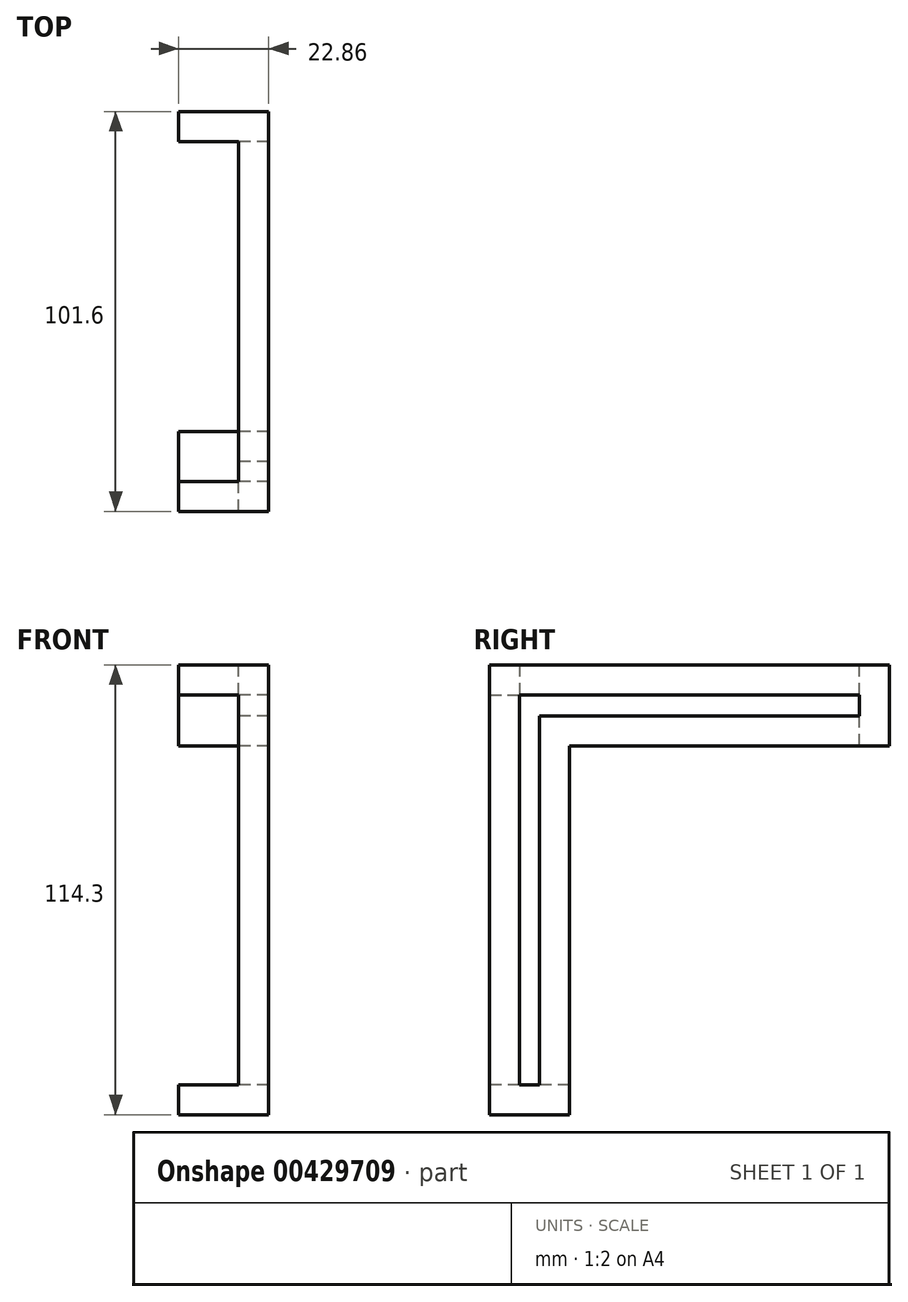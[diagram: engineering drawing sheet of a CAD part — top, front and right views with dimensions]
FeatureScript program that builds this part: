
annotation { "Feature Type Name" : "Feature", "Feature Type Description" : "" }
export const myFeature = defineFeature(function(context is Context, id is Id, definition is map)
    precondition{}
    {
        {
            var Q0;
            Q0=qCreatedBy(makeId("Right.planeOp"),FACE);
            var sketch = newSketch(context, id + "F0", { "sketchPlane" : qUnion([Q0])});
            skLineSegment(sketch, "E0.bottom", {"start": v(0, -114.3) * mm, "end": v(20.32, -114.3) * mm});
            skLineSegment(sketch, "E0.top", {"start": v(0, 0) * mm, "end": v(20.32, 0) * mm});
            skLineSegment(sketch, "E0.left", {"start": v(0, -114.3) * mm, "end": v(0, 0) * mm});
            skLineSegment(sketch, "E0.right", {"start": v(20.32, -114.3) * mm, "end": v(20.32, -20.57) * mm});
            skLineSegment(sketch, "E1.bottom", {"start": v(0, 0) * mm, "end": v(101.6, 0) * mm});
            skLineSegment(sketch, "E1.top", {"start": v(20.32, -20.57) * mm, "end": v(101.6, -20.57) * mm});
            skLineSegment(sketch, "E1.right", {"start": v(101.6, 0) * mm, "end": v(101.6, -20.57) * mm});
            skLineSegment(sketch, "E2", {"start": v(7.62, -106.68) * mm, "end": v(7.62, -7.62) * mm});
            skLineSegment(sketch, "E3", {"start": v(7.62, -7.62) * mm, "end": v(93.98, -7.62) * mm});
            skLineSegment(sketch, "E4", {"start": v(93.98, -7.62) * mm, "end": v(93.98, -12.95) * mm});
            skLineSegment(sketch, "E5", {"start": v(93.98, -12.95) * mm, "end": v(12.7, -12.95) * mm});
            skLineSegment(sketch, "E6", {"start": v(12.7, -12.95) * mm, "end": v(12.7, -106.68) * mm});
            skLineSegment(sketch, "E7", {"start": v(12.7, -106.68) * mm, "end": v(7.62, -106.68) * mm});
            skSolve(sketch);
        }
        {
            var Q0;
            Q0=makeQuery(id+"F0.imprint","IMPRINT",FACE,{"disambiguationData":[TD([[makeQuery(id+"F0.imprint","IMPRINT",EDGE,{"derivedFrom":sQuery(id+"F0.wireOp",EDGE,"E0.bottom")}),1.0]])]});
            extrude(context, id + "F1", {"entities" : qUnion([Q0]), "depth" : 22.86 * mm});
        }
        {
            var Q0;
            Q0=makeQuery(id+"F1.opExtrude","SWEPT_FACE",FACE,{"disambiguationData":[OSD([sQuery(id+"F0.wireOp",EDGE,"E1.bottom")])]});
            var sketch = newSketch(context, id + "F2", { "sketchPlane" : qUnion([Q0])});
            skLineSegment(sketch, "E8.bottom", {"start": v(0, 93.98) * mm, "end": v(15.24, 93.98) * mm});
            skLineSegment(sketch, "E8.top", {"start": v(0, -25.4) * mm, "end": v(15.24, -25.4) * mm});
            skLineSegment(sketch, "E8.left", {"start": v(0, 93.98) * mm, "end": v(0, -25.4) * mm});
            skLineSegment(sketch, "E8.right", {"start": v(15.24, 93.98) * mm, "end": v(15.24, -25.4) * mm});
            skSolve(sketch);
        }
        {
            var Q0;
            Q0 = qSketchRegion(id + "F2", true);
            extrude(context, id + "F3", {"entities" : qUnion([Q0]), "operationType" : NewBodyOperationType.REMOVE, "oppositeDirection" : true, "depth" : 106.68 * mm});
        }
        {
            var Q0;
            {var subQ0=sQuery(id+"F2.wireOp",EDGE,"E8.right");Q0=makeQuery(id+"F3.boolean.opBoolean","COPY",FACE,{"disambiguationData":[TD([makeQuery(id+"F1.opExtrude","SWEPT_FACE",FACE,{"disambiguationData":[OSD([sQuery(id+"F0.wireOp",EDGE,"E0.left")])]})])],"derivedFrom":makeQuery(id+"F3.opExtrude","SWEPT_FACE",FACE,{"disambiguationData":[OSD([subQ0])]})});}
            var sketch = newSketch(context, id + "F4", { "sketchPlane" : qUnion([Q0])});
            skLineSegment(sketch, "E9.bottom", {"start": v(0, 0) * mm, "end": v(-7.62, 0) * mm});
            skLineSegment(sketch, "E9.top", {"start": v(0, -7.62) * mm, "end": v(-7.62, -7.62) * mm});
            skLineSegment(sketch, "E9.left", {"start": v(0, 0) * mm, "end": v(0, -7.62) * mm});
            skLineSegment(sketch, "E9.right", {"start": v(-7.62, 0) * mm, "end": v(-7.62, -7.62) * mm});
            skSolve(sketch);
        }
        {
            var Q0;
            Q0 = qSketchRegion(id + "F4", true);
            var Q1;
            {var subQ0=sQuery(id+"F0.wireOp",EDGE,"E1.right");var subQ1=sQuery(id+"F0.wireOp",EDGE,"E1.top");var subQ2=sQuery(id+"F0.wireOp",EDGE,"E4");var subQ3=sQuery(id+"F0.wireOp",EDGE,"E1.bottom");Q1=makeQuery(id+"F3.boolean.opBoolean","SPLIT",FACE,{"disambiguationData":[TD([makeQuery(id+"F1.opExtrude","SWEPT_FACE",FACE,{"disambiguationData":[OSD([subQ3])]})])],"derivedFrom":makeQuery(id+"F1.opExtrude","CAP_FACE",FACE,{"disambiguationData":[OSD([sQuery(id+"F0.wireOp",EDGE,"E0.bottom"),sQuery(id+"F0.wireOp",EDGE,"E0.left"),sQuery(id+"F0.wireOp",EDGE,"E0.right"),subQ3,subQ1,subQ0,sQuery(id+"F0.wireOp",EDGE,"E2"),sQuery(id+"F0.wireOp",EDGE,"E3"),subQ2,sQuery(id+"F0.wireOp",EDGE,"E5"),sQuery(id+"F0.wireOp",EDGE,"E6"),sQuery(id+"F0.wireOp",EDGE,"E7")])],"isStart":true})});}
            extrude(context, id + "F5", {"entities" : qUnion([Q0]), "operationType" : NewBodyOperationType.ADD, "endBound" : BoundingType.UP_TO_SURFACE, "endBoundEntityFace" : qUnion([Q1]), "depth" : 25.4 * mm});
        }
    });
